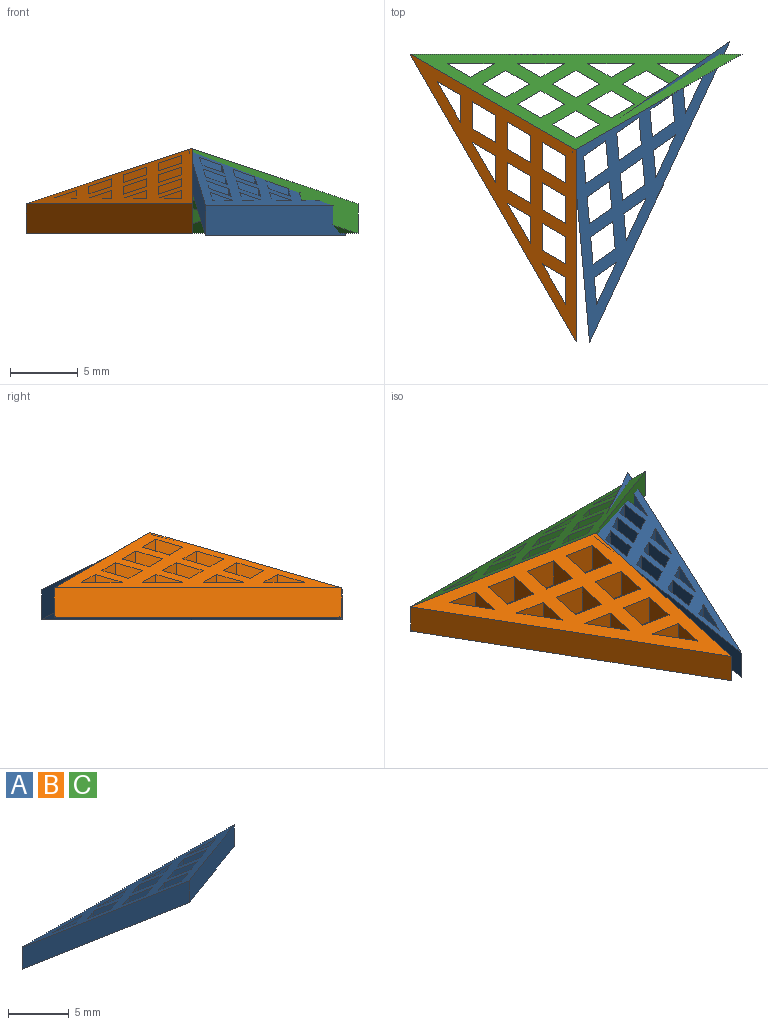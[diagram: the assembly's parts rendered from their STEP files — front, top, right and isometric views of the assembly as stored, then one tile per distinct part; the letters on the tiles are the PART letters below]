
ASSEMBLY  parts=3 mates=1
PART A: 41 faces, bbox 24.6x7.1x6.3 mm
  f0: plane 24.6x7.1mm, normal (0,0.5,0.87), area 68.8mm2, adj f2,f3,f4,f5,f6,f7,f8,f9
  f1: plane 24.6x7.1mm, normal (0,-0.5,-0.87), area 68.8mm2, adj f2,f3,f4,f5,f6,f7,f8,f9
  f2: plane 12.3x7.1mm, normal (0.5,-0.87,0), area 31.2mm2, adj f0,f1,f3,f4
  f3: plane 12.3x7.1mm, normal (-0.5,-0.87,0), area 31.2mm2, adj f0,f1,f2,f4
  f4: plane 24.6x2.19mm, normal (0,1,0), area 54mm2, adj f0,f1,f2,f3
  f5: plane 2.77x1.73mm, normal (0.5,0.87,0), area 4.4mm2, adj f0,f1,f6,f8
  f6: plane 2.77x1.73mm, normal (-0.5,0.87,0), area 4.4mm2, adj f0,f1,f5,f7
  f7: plane 2.77x1.73mm, normal (-0.5,-0.87,0), area 4.4mm2, adj f0,f1,f6,f8
  f8: plane 2.77x1.73mm, normal (0.5,-0.87,0), area 4.4mm2, adj f0,f1,f5,f7
  f9: plane 2.77x1.73mm, normal (0.5,0.87,0), area 4.4mm2, adj f0,f1,f10,f11
  f10: plane 2.77x1.73mm, normal (-0.5,0.87,0), area 4.4mm2, adj f0,f1,f9,f11
  f11: plane 3.46x2.19mm, normal (0,-1,0), area 7.6mm2, adj f0,f1,f9,f10
  f12: plane 2.77x1.73mm, normal (0.5,0.87,0), area 4.4mm2, adj f0,f1,f13,f15
  f13: plane 2.77x1.73mm, normal (-0.5,0.87,0), area 4.4mm2, adj f0,f1,f12,f14
  f14: plane 2.77x1.73mm, normal (-0.5,-0.87,0), area 4.4mm2, adj f0,f1,f13,f15
  f15: plane 2.77x1.73mm, normal (0.5,-0.87,0), area 4.4mm2, adj f0,f1,f12,f14
  f16: plane 2.77x1.73mm, normal (0.5,0.87,0), area 4.4mm2, adj f0,f1,f17,f18
  f17: plane 2.77x1.73mm, normal (-0.5,0.87,0), area 4.4mm2, adj f0,f1,f16,f18
  f18: plane 3.46x2.19mm, normal (0,-1,0), area 7.6mm2, adj f0,f1,f16,f17
  f19: plane 2.77x1.73mm, normal (0.5,0.87,0), area 4.4mm2, adj f0,f1,f20,f22
  f20: plane 2.77x1.73mm, normal (-0.5,0.87,0), area 4.4mm2, adj f0,f1,f19,f21
  f21: plane 2.77x1.73mm, normal (-0.5,-0.87,0), area 4.4mm2, adj f0,f1,f20,f22
  f22: plane 2.77x1.73mm, normal (0.5,-0.87,0), area 4.4mm2, adj f0,f1,f19,f21
  f23: plane 2.77x1.73mm, normal (0.5,0.87,0), area 4.4mm2, adj f0,f1,f24,f26
  f24: plane 2.77x1.73mm, normal (-0.5,0.87,0), area 4.4mm2, adj f0,f1,f23,f25
  f25: plane 2.77x1.73mm, normal (-0.5,-0.87,0), area 4.4mm2, adj f0,f1,f24,f26
  f26: plane 2.77x1.73mm, normal (0.5,-0.87,0), area 4.4mm2, adj f0,f1,f23,f25
  f27: plane 2.77x1.73mm, normal (0.5,0.87,0), area 4.4mm2, adj f0,f1,f28,f29
  f28: plane 2.77x1.73mm, normal (-0.5,0.87,0), area 4.4mm2, adj f0,f1,f27,f29
  f29: plane 3.46x2.19mm, normal (0,-1,0), area 7.6mm2, adj f0,f1,f27,f28
  f30: plane 2.77x1.73mm, normal (0.5,0.87,0), area 4.4mm2, adj f0,f1,f31,f33
  f31: plane 2.77x1.73mm, normal (-0.5,0.87,0), area 4.4mm2, adj f0,f1,f30,f32
  f32: plane 2.77x1.73mm, normal (-0.5,-0.87,0), area 4.4mm2, adj f0,f1,f31,f33
  f33: plane 2.77x1.73mm, normal (0.5,-0.87,0), area 4.4mm2, adj f0,f1,f30,f32
  f34: plane 2.77x1.73mm, normal (0.5,0.87,0), area 4.4mm2, adj f0,f1,f35,f36
  f35: plane 2.77x1.73mm, normal (-0.5,0.87,0), area 4.4mm2, adj f0,f1,f34,f36
  f36: plane 3.46x2.19mm, normal (0,-1,0), area 7.6mm2, adj f0,f1,f34,f35
  f37: plane 2.77x1.73mm, normal (0.5,0.87,0), area 4.4mm2, adj f0,f1,f38,f40
  f38: plane 2.77x1.73mm, normal (-0.5,0.87,0), area 4.4mm2, adj f0,f1,f37,f39
  f39: plane 2.77x1.73mm, normal (-0.5,-0.87,0), area 4.4mm2, adj f0,f1,f38,f40
  f40: plane 2.77x1.73mm, normal (0.5,-0.87,0), area 4.4mm2, adj f0,f1,f37,f39
PART B: same geometry as A
PART C: same geometry as A
PLACE A rot(axis=(0,0,-1),115deg) t=(34.6,-6.98,-2.44)mm
PLACE B rot(axis=(0,0,1),120deg) t=(34.83,-6.86,-2.29)mm
PLACE C t=(34.83,-6.86,-2.29)mm
MATE planar B.f2 <-> C.f3  axis (0.5,0.87,0) through (28.68,-3.31,-5.43)mm
